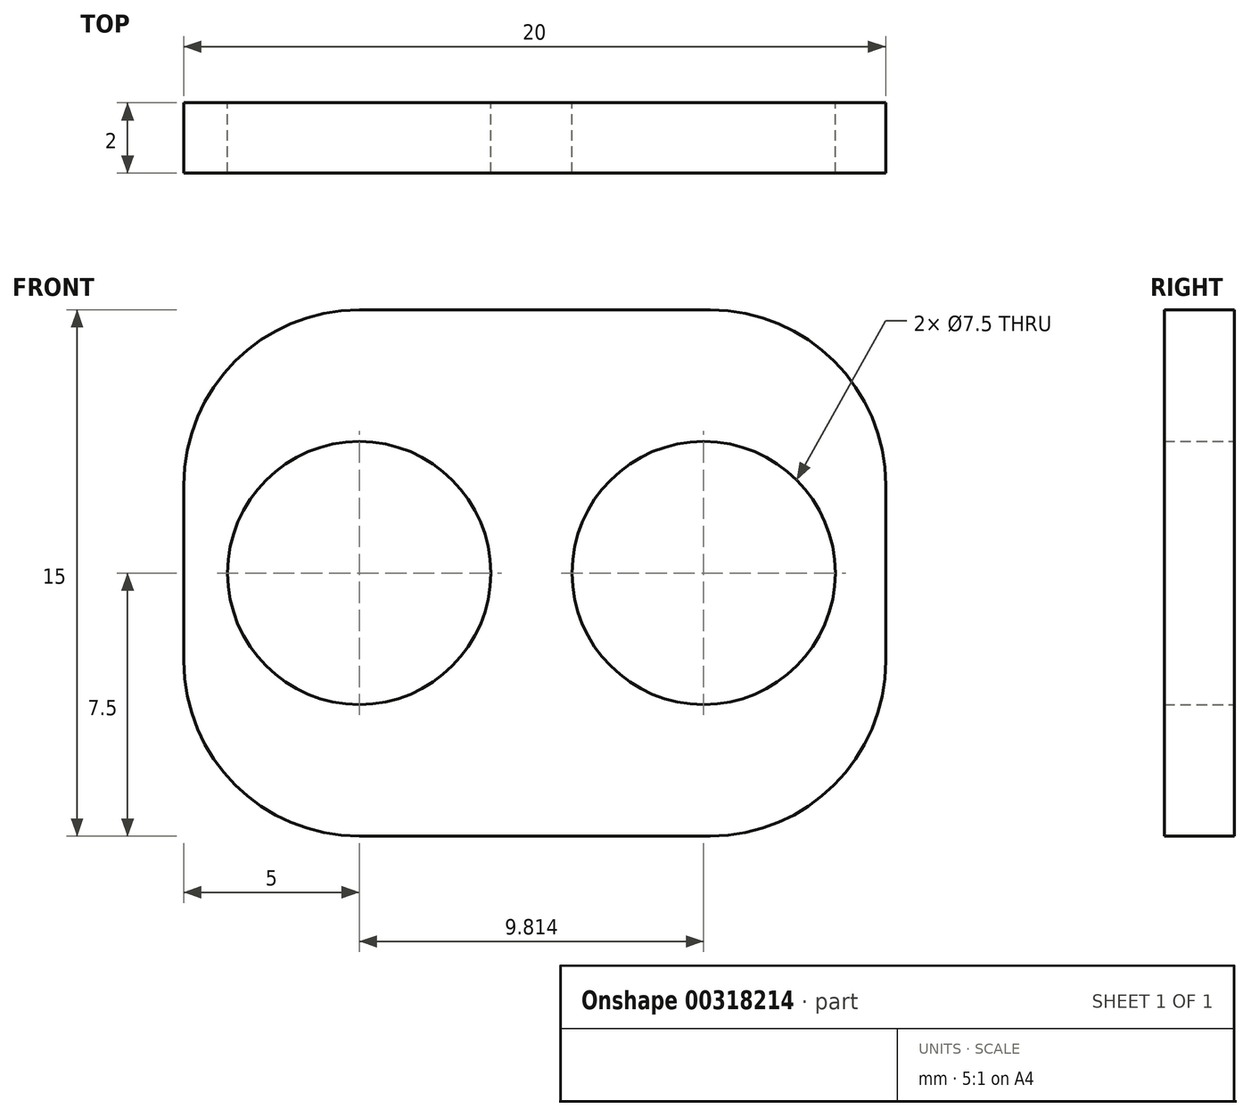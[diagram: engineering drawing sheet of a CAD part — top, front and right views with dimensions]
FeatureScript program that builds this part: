
annotation { "Feature Type Name" : "Feature", "Feature Type Description" : "" }
export const myFeature = defineFeature(function(context is Context, id is Id, definition is map)
    precondition{}
    {
        {
            var Q0;
            Q0=qCreatedBy(makeId("Front.planeOp"),FACE);
            var sketch = newSketch(context, id + "F0", { "sketchPlane" : qUnion([Q0])});
            skLineSegment(sketch, "E0.bottom", {"start": v(5, 7.5) * mm, "end": v(-5, 7.5) * mm});
            skLineSegment(sketch, "E0.top", {"start": v(5, -7.5) * mm, "end": v(-5, -7.5) * mm});
            skLineSegment(sketch, "E0.left", {"start": v(10, 2.5) * mm, "end": v(10, -2.5) * mm});
            skLineSegment(sketch, "E0.right", {"start": v(-10, 2.5) * mm, "end": v(-10, -2.5) * mm});
            skPoint(sketch, "E0.middle", {"position": v(0, 0) * mm});
            skPoint(sketch, "E1.visualSharp", {"position": v(-10, 7.5) * mm});
            skArc(sketch, "E1.filletArc", {"start": v(-5, 7.5) * mm, "mid": v(-8.54, 6.04) * mm, "end": v(-10, 2.5) * mm});
            skPoint(sketch, "E2.visualSharp", {"position": v(-10, -7.5) * mm});
            skArc(sketch, "E2.filletArc", {"start": v(-10, -2.5) * mm, "mid": v(-8.54, -6.04) * mm, "end": v(-5, -7.5) * mm});
            skPoint(sketch, "E3.visualSharp", {"position": v(10, -7.5) * mm});
            skArc(sketch, "E3.filletArc", {"start": v(5, -7.5) * mm, "mid": v(8.54, -6.04) * mm, "end": v(10, -2.5) * mm});
            skPoint(sketch, "E4.visualSharp", {"position": v(10, 7.5) * mm});
            skArc(sketch, "E4.filletArc", {"start": v(10, 2.5) * mm, "mid": v(8.54, 6.04) * mm, "end": v(5, 7.5) * mm});
            skCircle(sketch, "E5", {"center": v(-5, 0) * mm, "radius": 3.75 * mm});
            skCircle(sketch, "E6", {"center": v(4.81, 0) * mm, "radius": 3.75 * mm});
            skSolve(sketch);
        }
        {
            var Q0;
            Q0=makeQuery(id+"F0.imprint","IMPRINT",FACE,{"disambiguationData":[TD([[makeQuery(id+"F0.imprint","IMPRINT",EDGE,{"derivedFrom":sQuery(id+"F0.wireOp",EDGE,"E0.bottom")}),1.0]])]});
            extrude(context, id + "F1", {"entities" : qUnion([Q0]), "depth" : 2 * mm});
        }
    });
